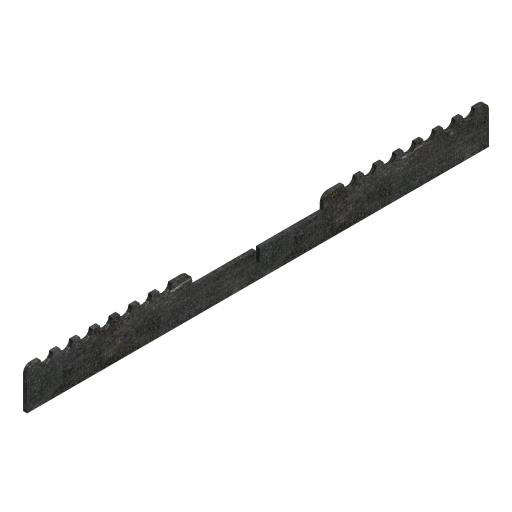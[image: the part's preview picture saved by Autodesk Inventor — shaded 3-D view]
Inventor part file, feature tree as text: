
AUTODESK INVENTOR PART (.ipt)
format: ipt  version: 2024.3 (Build 283343000, 343)  size: 215,040 bytes
history: native  units: mm
features: extrude x2, sketch x2, fillet x1, mirror x1
ambient origin geometry x8: Origin, YZ Plane, XZ Plane, XY Plane, X Axis, Y Axis, Z Axis, Center Point
bodies: Solid1 (feature_tree)
feature tree (6):
  extrude  "Extrusion1"  Depth=350.0mm
  extrude  "Extrusion2"  Depth=100.0mm
  fillet  "Fillet1"  Radius=20.0mm
  mirror  "Mirror1"
  sketch  "Sketch1"  dims[d0=30.0mm d1=350.0mm]
  sketch  "Sketch2"  dims[d2=0.0mm d3=100.0mm d4=20.0mm d5=20.0mm d6=3.1mm d7=3.0mm d8=0.0mm d9=10.0mm d10=10.0mm d11=10.0mm d12=10.0mm d13=10.0mm d14=10.0mm d15=10.0mm d16=15.0mm d17=15.0mm d18=15.0mm d19=15.0mm d20=15.0mm d21=15.0mm d22=15.0mm d23=3.0mm d24=0.0mm d25=5.0mm]
